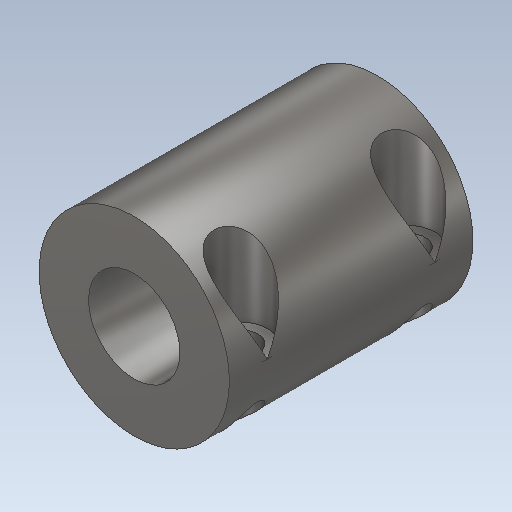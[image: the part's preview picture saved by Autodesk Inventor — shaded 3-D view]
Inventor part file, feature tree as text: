
AUTODESK INVENTOR PART (.ipt)
format: ipt  version: 2020 (Build 240168000, 168)  size: 188,416 bytes
history: native  units: mm
features: extrude x4, sketch x4, other x1
ambient origin geometry x8: Origin, YZ Plane, XZ Plane, XY Plane, X Axis, Y Axis, Z Axis, Center Point
bodies: Body1 (feature_tree)
feature tree (9):
  other  "Bryła1"
  extrude  "Wyciągnięcie proste1"  Depth=25.0mm
  extrude  "Wyciągnięcie proste2"  Depth=32.0mm TaperAngle=0.0deg
  extrude  "Wyciągnięcie proste3"  Depth=12.0mm
  extrude  "Wyciągnięcie proste4"  Depth=32.0mm TaperAngle=0.0deg
  sketch  "Szkic1"
  sketch  "Szkic2"
  sketch  "Szkic3"
  sketch  "Szkic4"
